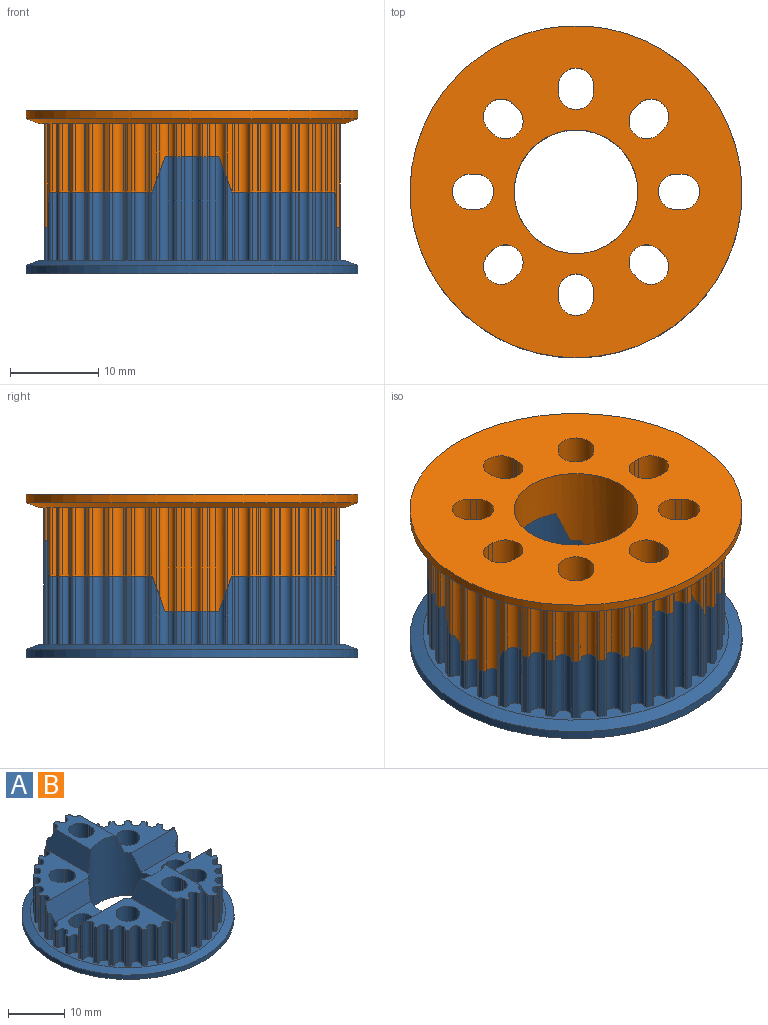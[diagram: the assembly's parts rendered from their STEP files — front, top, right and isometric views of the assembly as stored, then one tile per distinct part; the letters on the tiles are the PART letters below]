
ASSEMBLY  parts=2 mates=1
PART A: 233 faces, bbox 37.6x37.6x13.3 mm
  f0: cylinder r=2mm len=5.25mm, axis (0,0,-1), area 33mm2, adj f49,f55,f231,f232
  f1: cylinder r=2mm len=9.25mm, axis (0,0,-1), area 58.1mm2, adj f49,f53,f226,f227
  f2: cylinder r=2mm len=9.25mm, axis (0,0,-1), area 58.1mm2, adj f49,f61,f212,f213
  f3: cone r=18.8mm half-angle=70deg, axis (0,0,-1), area 181mm2, adj f4,f211
  f4: cylinder r=18.8mm len=37.6mm, axis (0,0,1), area 112.7mm2, adj f3,f49
  f5: cylinder r=0.86mm len=11.75mm, axis (0,0,1), area 17.8mm2, adj f30,f36,f59,f211
  f6: cylinder r=0.27mm len=11.75mm, axis (0,0,1), area 5.4mm2, adj f36,f59,f148,f211
  f7: cylinder r=0.27mm len=11.75mm, axis (0,0,1), area 5.4mm2, adj f29,f59,f147,f211
  f8: cylinder r=0.86mm len=11.75mm, axis (0,0,1), area 17.8mm2, adj f28,f59,f76,f211
  f9: cylinder r=0.27mm len=7.75mm, axis (0,0,1), area 3.6mm2, adj f31,f52,f141,f211
  f10: cylinder r=0.86mm len=7.75mm, axis (0,0,1), area 11.7mm2, adj f35,f61,f96,f211
  f11: cylinder r=0.27mm len=7.75mm, axis (0,0,1), area 3.6mm2, adj f26,f52,f151,f211
  f12: cylinder r=0.86mm len=7.75mm, axis (0,0,1), area 11.7mm2, adj f37,f61,f95,f211
  f13: cylinder r=0.27mm len=7.75mm, axis (0,0,1), area 3.6mm2, adj f27,f52,f155,f211
  f14: cylinder r=0.86mm len=7.75mm, axis (0,0,1), area 11.7mm2, adj f38,f61,f94,f211
  f15: cylinder r=0.27mm len=7.75mm, axis (0,0,1), area 3.6mm2, adj f33,f52,f159,f211
  f16: cylinder r=0.86mm len=7.75mm, axis (0,0,1), area 11.7mm2, adj f39,f61,f93,f211
  f17: cylinder r=0.27mm len=7.75mm, axis (0,0,1), area 3.6mm2, adj f34,f52,f163,f211
  f18: cylinder r=0.86mm len=7.75mm, axis (0,0,1), area 11.7mm2, adj f40,f61,f92,f211
  f19: cylinder r=0.27mm len=7.75mm, axis (0,0,1), area 3.6mm2, adj f32,f52,f167,f211
  f20: cylinder r=0.86mm len=7.75mm, axis (0,0,1), area 11.7mm2, adj f41,f61,f91,f211
  f21: cylinder r=0.27mm len=6.55mm, axis (0,0,1), area 2.8mm2, adj f43,f119,f138,f211
  f22: cylinder r=0.86mm len=5.64mm, axis (0,0,1), area 7.1mm2, adj f44,f55,f69,f122,f211
  f23: cylinder r=0.27mm len=3.75mm, axis (0,0,1), area 1.7mm2, adj f42,f54,f134,f211
  f24: cylinder r=0.86mm len=3.75mm, axis (0,0,1), area 5.7mm2, adj f45,f55,f67,f211
  f25: cylinder r=7mm len=14mm, axis (0,0,-1), area 406.8mm2, adj f49,f50,f51,f52,f53,f54,f55,f59
  f26: cylinder r=0.86mm len=7.75mm, axis (0,0,-1), area 11.7mm2, adj f11,f52,f153,f211
  f27: cylinder r=0.86mm len=7.75mm, axis (0,0,-1), area 11.7mm2, adj f13,f52,f157,f211
  f28: cylinder r=0.27mm len=11.75mm, axis (0,0,-1), area 5.4mm2, adj f8,f59,f148,f211
  f29: cylinder r=0.86mm len=11.75mm, axis (0,0,-1), area 17.8mm2, adj f7,f59,f142,f211
  f30: cylinder r=0.27mm len=11.75mm, axis (0,0,-1), area 5.4mm2, adj f5,f59,f147,f211
  f31: cylinder r=0.86mm len=7.75mm, axis (0,0,-1), area 11.7mm2, adj f9,f52,f149,f211
  f32: cylinder r=0.86mm len=7.75mm, axis (0,0,-1), area 11.7mm2, adj f19,f52,f169,f211
  f33: cylinder r=0.86mm len=7.75mm, axis (0,0,-1), area 11.7mm2, adj f15,f52,f161,f211
  f34: cylinder r=0.86mm len=7.75mm, axis (0,0,-1), area 11.7mm2, adj f17,f52,f165,f211
  f35: cylinder r=0.27mm len=7.75mm, axis (0,0,-1), area 3.6mm2, adj f10,f61,f145,f211
  f36: cylinder r=0.86mm len=11.75mm, axis (0,0,-1), area 17.8mm2, adj f5,f6,f59,f211
  f37: cylinder r=0.27mm len=7.75mm, axis (0,0,-1), area 3.6mm2, adj f12,f61,f152,f211
  f38: cylinder r=0.27mm len=7.75mm, axis (0,0,-1), area 3.6mm2, adj f14,f61,f156,f211
  f39: cylinder r=0.27mm len=7.75mm, axis (0,0,-1), area 3.6mm2, adj f16,f61,f160,f211
  f40: cylinder r=0.27mm len=7.75mm, axis (0,0,-1), area 3.6mm2, adj f18,f61,f164,f211
  f41: cylinder r=0.27mm len=7.75mm, axis (0,0,-1), area 3.6mm2, adj f20,f61,f168,f211
  f42: cylinder r=0.86mm len=3.75mm, axis (0,0,-1), area 5.7mm2, adj f23,f54,f132,f211
  f43: cylinder r=0.86mm len=5.64mm, axis (0,0,-1), area 7.1mm2, adj f21,f54,f119,f136,f211
  f44: cylinder r=0.27mm len=6.55mm, axis (0,0,-1), area 2.8mm2, adj f22,f122,f137,f211
  f45: cylinder r=0.27mm len=3.75mm, axis (0,0,-1), area 1.7mm2, adj f24,f55,f133,f211
  f46: cylinder r=2mm len=9.25mm, axis (0,0,-1), area 58.1mm2, adj f49,f52,f218,f219
  f47: cylinder r=2mm len=9.25mm, axis (0,0,-1), area 58.1mm2, adj f49,f51,f221,f222
  f48: cylinder r=2mm len=5.25mm, axis (0,0,-1), area 33mm2, adj f49,f54,f228,f230
  f49: plane 37.6x37.6mm, normal (0,0,-1), area 833.9mm2, adj f0,f1,f2,f4,f25,f46,f47,f48
  f50: plane 10.46x6.09mm, normal (0,0,1), area 40.4mm2, adj f25,f58,f63,f64,f65,f75,f86,f115
  f51: plane 11.69x11.69mm, normal (0,0,1), area 64.5mm2, adj f25,f47,f103,f104,f105,f106,f107,f108
  f52: plane 11.69x11.69mm, normal (0,0,1), area 64.5mm2, adj f9,f11,f13,f15,f17,f19,f25,f26
  f53: plane 11.69x11.69mm, normal (0,0,1), area 64.5mm2, adj f1,f25,f57,f78,f79,f80,f81,f82
  f54: plane 10.46x6.09mm, normal (0,0,1), area 40.4mm2, adj f23,f25,f42,f43,f48,f71,f72,f73
  f55: plane 10.46x6.09mm, normal (0,0,1), area 40.4mm2, adj f0,f22,f24,f25,f45,f56,f66,f67
  f56: cylinder r=2mm len=5.25mm, axis (0,0,-1), area 33mm2, adj f49,f55,f231,f232
  f57: cylinder r=2mm len=9.25mm, axis (0,0,-1), area 58.1mm2, adj f49,f53,f226,f227
  f58: cylinder r=2mm len=13.25mm, axis (0,0,-1), area 83.3mm2, adj f49,f50,f223,f225
  f59: plane 10.46x6.09mm, normal (0,0,1), area 40.4mm2, adj f5,f6,f7,f8,f25,f28,f29,f30
  f60: cylinder r=2mm len=13.25mm, axis (0,0,-1), area 83.3mm2, adj f49,f59,f214,f216
  f61: plane 11.69x11.69mm, normal (0,0,1), area 64.5mm2, adj f2,f10,f12,f14,f16,f18,f20,f25
  f62: cylinder r=2mm len=9.25mm, axis (0,0,-1), area 58.1mm2, adj f49,f61,f212,f213
  f63: cylinder r=0.86mm len=11.75mm, axis (0,0,-1), area 17.8mm2, adj f50,f209,f210,f211
  f64: cylinder r=0.27mm len=11.75mm, axis (0,0,-1), area 5.4mm2, adj f50,f205,f207,f211
  f65: cylinder r=0.86mm len=11.75mm, axis (0,0,-1), area 17.8mm2, adj f50,f143,f206,f211
  f66: cylinder r=0.27mm len=3.75mm, axis (0,0,-1), area 1.7mm2, adj f55,f127,f129,f211
  f67: cylinder r=0.86mm len=3.75mm, axis (0,0,-1), area 5.7mm2, adj f24,f55,f131,f211
  f68: cylinder r=0.86mm len=5.64mm, axis (0,0,-1), area 7.1mm2, adj f55,f121,f125,f127,f211
  f69: cylinder r=0.86mm len=3.75mm, axis (0,0,-1), area 5.7mm2, adj f22,f55,f135,f211
  f70: cylinder r=0.27mm len=6.55mm, axis (0,0,-1), area 2.8mm2, adj f120,f124,f126,f211
  f71: cylinder r=0.27mm len=3.75mm, axis (0,0,-1), area 1.7mm2, adj f54,f130,f132,f211
  f72: cylinder r=0.86mm len=3.75mm, axis (0,0,-1), area 5.7mm2, adj f54,f126,f128,f211
  f73: cylinder r=0.27mm len=3.75mm, axis (0,0,-1), area 1.7mm2, adj f54,f134,f136,f211
  f74: cylinder r=0.27mm len=9.86mm, axis (0,0,-1), area 4.4mm2, adj f118,f141,f142,f211
  f75: cylinder r=0.86mm len=11.75mm, axis (0,0,-1), area 16.4mm2, adj f50,f117,f139,f205,f211
  f76: cylinder r=0.86mm len=11.75mm, axis (0,0,-1), area 16.4mm2, adj f8,f59,f116,f146,f211
  f77: cylinder r=0.27mm len=9.86mm, axis (0,0,-1), area 4.4mm2, adj f115,f143,f144,f211
  f78: cylinder r=0.86mm len=7.75mm, axis (0,0,-1), area 11.7mm2, adj f53,f172,f174,f211
  f79: cylinder r=0.27mm len=7.75mm, axis (0,0,-1), area 3.6mm2, adj f53,f182,f184,f211
  f80: cylinder r=0.86mm len=7.75mm, axis (0,0,-1), area 11.7mm2, adj f53,f178,f180,f211
  f81: cylinder r=0.27mm len=7.75mm, axis (0,0,-1), area 3.6mm2, adj f53,f188,f190,f211
  f82: cylinder r=0.27mm len=7.75mm, axis (0,0,-1), area 3.6mm2, adj f53,f123,f172,f211
  f83: cylinder r=0.27mm len=7.75mm, axis (0,0,-1), area 3.6mm2, adj f53,f176,f178,f211
  f84: cylinder r=0.86mm len=7.75mm, axis (0,0,-1), area 11.7mm2, adj f53,f196,f198,f211
  f85: cylinder r=0.86mm len=7.75mm, axis (0,0,-1), area 11.7mm2, adj f53,f202,f204,f211
  f86: cylinder r=0.27mm len=11.75mm, axis (0,0,-1), area 5.4mm2, adj f50,f208,f210,f211
  f87: cylinder r=0.86mm len=7.75mm, axis (0,0,-1), area 11.7mm2, adj f53,f184,f186,f211
  f88: cylinder r=0.27mm len=7.75mm, axis (0,0,-1), area 3.6mm2, adj f53,f194,f196,f211
  f89: cylinder r=0.86mm len=7.75mm, axis (0,0,-1), area 11.7mm2, adj f53,f190,f192,f211
  f90: cylinder r=0.27mm len=7.75mm, axis (0,0,-1), area 3.6mm2, adj f53,f200,f202,f211
  f91: cylinder r=0.86mm len=7.75mm, axis (0,0,-1), area 11.7mm2, adj f20,f61,f170,f211
  f92: cylinder r=0.86mm len=7.75mm, axis (0,0,-1), area 11.7mm2, adj f18,f61,f166,f211
  f93: cylinder r=0.86mm len=7.75mm, axis (0,0,-1), area 11.7mm2, adj f16,f61,f162,f211
  f94: cylinder r=0.86mm len=7.75mm, axis (0,0,-1), area 11.7mm2, adj f14,f61,f158,f211
  f95: cylinder r=0.86mm len=7.75mm, axis (0,0,-1), area 11.7mm2, adj f12,f61,f154,f211
  f96: cylinder r=0.86mm len=7.75mm, axis (0,0,-1), area 11.7mm2, adj f10,f61,f150,f211
  f97: cylinder r=0.27mm len=7.75mm, axis (0,0,-1), area 3.6mm2, adj f52,f157,f159,f211
  f98: cylinder r=0.27mm len=7.75mm, axis (0,0,-1), area 3.6mm2, adj f52,f153,f155,f211
  f99: cylinder r=0.27mm len=7.75mm, axis (0,0,-1), area 3.6mm2, adj f52,f138,f169,f211
  f100: cylinder r=0.27mm len=7.75mm, axis (0,0,-1), area 3.6mm2, adj f52,f165,f167,f211
  f101: cylinder r=0.27mm len=7.75mm, axis (0,0,-1), area 3.6mm2, adj f52,f161,f163,f211
  f102: cylinder r=0.27mm len=7.75mm, axis (0,0,-1), area 3.6mm2, adj f52,f149,f151,f211
  f103: cylinder r=0.86mm len=7.75mm, axis (0,0,-1), area 11.7mm2, adj f51,f195,f197,f211
  f104: cylinder r=0.27mm len=7.75mm, axis (0,0,-1), area 3.6mm2, adj f51,f185,f187,f211
  f105: cylinder r=0.86mm len=7.75mm, axis (0,0,-1), area 11.7mm2, adj f51,f189,f191,f211
  f106: cylinder r=0.27mm len=7.75mm, axis (0,0,-1), area 3.6mm2, adj f51,f179,f181,f211
  f107: cylinder r=0.27mm len=7.75mm, axis (0,0,-1), area 3.6mm2, adj f51,f140,f203,f211
  f108: cylinder r=0.27mm len=7.75mm, axis (0,0,-1), area 3.6mm2, adj f51,f197,f199,f211
  f109: cylinder r=0.86mm len=7.75mm, axis (0,0,-1), area 11.7mm2, adj f51,f201,f203,f211
  f110: cylinder r=0.27mm len=7.75mm, axis (0,0,-1), area 3.6mm2, adj f51,f191,f193,f211
  f111: cylinder r=0.86mm len=7.75mm, axis (0,0,-1), area 11.7mm2, adj f51,f177,f179,f211
  f112: cylinder r=0.27mm len=7.75mm, axis (0,0,-1), area 3.6mm2, adj f51,f173,f175,f211
  f113: cylinder r=0.86mm len=7.75mm, axis (0,0,-1), area 11.7mm2, adj f51,f183,f185,f211
  f114: cylinder r=0.86mm len=7.75mm, axis (0,0,-1), area 11.7mm2, adj f51,f171,f173,f211
  f115: plane 10.95x4mm, normal (-0.94,0,0.34), area 42.6mm2, adj f25,f50,f53,f77,f143,f144
  f116: plane 10.98x4mm, normal (-0.94,0,0.34), area 42.6mm2, adj f25,f59,f61,f76,f145,f146
  f117: plane 10.98x4mm, normal (0.94,0,0.34), area 42.6mm2, adj f25,f50,f51,f75,f139,f140
  f118: plane 10.95x4mm, normal (0.94,0,0.34), area 42.6mm2, adj f25,f52,f59,f74,f141,f142
  f119: plane 10.95x4mm, normal (0,-0.94,0.34), area 42.6mm2, adj f21,f25,f43,f52,f54,f138
  f120: plane 10.95x4mm, normal (0,0.94,0.34), area 42.6mm2, adj f25,f51,f54,f70,f124,f126
  f121: plane 10.95x4mm, normal (0,0.94,0.34), area 42.6mm2, adj f25,f53,f55,f68,f123,f125
  f122: plane 10.95x4mm, normal (0,-0.94,0.34), area 42.6mm2, adj f22,f25,f44,f55,f61,f137
  f123: cylinder r=16.8mm len=7.75mm, axis (0,0,-1), area 4.3mm2, adj f53,f82,f121,f125,f211
  f124: cylinder r=16.8mm len=7.75mm, axis (0,0,-1), area 4.3mm2, adj f51,f70,f120,f171,f211
  f125: cylinder r=0.27mm len=6.55mm, axis (0,0,1), area 2.8mm2, adj f68,f121,f123,f211
  f126: cylinder r=0.86mm len=5.64mm, axis (0,0,1), area 7.1mm2, adj f54,f70,f72,f120,f211
  f127: cylinder r=0.86mm len=3.75mm, axis (0,0,1), area 5.7mm2, adj f55,f66,f68,f211
  f128: cylinder r=0.27mm len=3.75mm, axis (0,0,1), area 1.7mm2, adj f54,f72,f130,f211
  f129: cylinder r=16.8mm len=3.75mm, axis (0,0,-1), area 2.2mm2, adj f55,f66,f131,f211
  f130: cylinder r=16.8mm len=3.75mm, axis (0,0,-1), area 2.2mm2, adj f54,f71,f128,f211
  f131: cylinder r=0.27mm len=3.75mm, axis (0,0,1), area 1.7mm2, adj f55,f67,f129,f211
  f132: cylinder r=0.86mm len=3.75mm, axis (0,0,1), area 5.7mm2, adj f42,f54,f71,f211
  f133: cylinder r=16.8mm len=3.75mm, axis (0,0,-1), area 2.2mm2, adj f45,f55,f135,f211
  f134: cylinder r=16.8mm len=3.75mm, axis (0,0,-1), area 2.2mm2, adj f23,f54,f73,f211
  f135: cylinder r=0.27mm len=3.75mm, axis (0,0,1), area 1.7mm2, adj f55,f69,f133,f211
  f136: cylinder r=0.86mm len=3.75mm, axis (0,0,1), area 5.7mm2, adj f43,f54,f73,f211
  f137: cylinder r=16.8mm len=7.75mm, axis (0,0,-1), area 4.3mm2, adj f44,f61,f122,f170,f211
  f138: cylinder r=16.8mm len=7.75mm, axis (0,0,-1), area 4.3mm2, adj f21,f52,f99,f119,f211
  f139: cylinder r=0.27mm len=9.86mm, axis (0,0,1), area 4.4mm2, adj f75,f117,f140,f211
  f140: cylinder r=16.8mm len=8.95mm, axis (0,0,-1), area 4.8mm2, adj f51,f107,f117,f139,f211
  f141: cylinder r=16.8mm len=8.95mm, axis (0,0,-1), area 4.8mm2, adj f9,f52,f74,f118,f211
  f142: cylinder r=0.86mm len=11.75mm, axis (0,0,1), area 16.4mm2, adj f29,f59,f74,f118,f211
  f143: cylinder r=0.86mm len=11.75mm, axis (0,0,1), area 16.4mm2, adj f50,f65,f77,f115,f211
  f144: cylinder r=16.8mm len=8.95mm, axis (0,0,-1), area 4.8mm2, adj f53,f77,f115,f204,f211
  f145: cylinder r=16.8mm len=8.95mm, axis (0,0,-1), area 4.8mm2, adj f35,f61,f116,f146,f211
  f146: cylinder r=0.27mm len=9.86mm, axis (0,0,1), area 4.4mm2, adj f76,f116,f145,f211
  f147: cylinder r=16.8mm len=11.75mm, axis (0,0,-1), area 6.9mm2, adj f7,f30,f59,f211
  f148: cylinder r=16.8mm len=11.75mm, axis (0,0,-1), area 6.9mm2, adj f6,f28,f59,f211
  f149: cylinder r=0.86mm len=7.75mm, axis (0,0,1), area 11.7mm2, adj f31,f52,f102,f211
  f150: cylinder r=0.27mm len=7.75mm, axis (0,0,1), area 3.6mm2, adj f61,f96,f152,f211
  f151: cylinder r=16.8mm len=7.75mm, axis (0,0,-1), area 4.5mm2, adj f11,f52,f102,f211
  f152: cylinder r=16.8mm len=7.75mm, axis (0,0,-1), area 4.5mm2, adj f37,f61,f150,f211
  f153: cylinder r=0.86mm len=7.75mm, axis (0,0,1), area 11.7mm2, adj f26,f52,f98,f211
  f154: cylinder r=0.27mm len=7.75mm, axis (0,0,1), area 3.6mm2, adj f61,f95,f156,f211
  f155: cylinder r=16.8mm len=7.75mm, axis (0,0,-1), area 4.5mm2, adj f13,f52,f98,f211
  f156: cylinder r=16.8mm len=7.75mm, axis (0,0,-1), area 4.5mm2, adj f38,f61,f154,f211
  f157: cylinder r=0.86mm len=7.75mm, axis (0,0,1), area 11.7mm2, adj f27,f52,f97,f211
  f158: cylinder r=0.27mm len=7.75mm, axis (0,0,1), area 3.6mm2, adj f61,f94,f160,f211
  f159: cylinder r=16.8mm len=7.75mm, axis (0,0,-1), area 4.5mm2, adj f15,f52,f97,f211
  f160: cylinder r=16.8mm len=7.75mm, axis (0,0,-1), area 4.5mm2, adj f39,f61,f158,f211
  f161: cylinder r=0.86mm len=7.75mm, axis (0,0,1), area 11.7mm2, adj f33,f52,f101,f211
  f162: cylinder r=0.27mm len=7.75mm, axis (0,0,1), area 3.6mm2, adj f61,f93,f164,f211
  f163: cylinder r=16.8mm len=7.75mm, axis (0,0,-1), area 4.5mm2, adj f17,f52,f101,f211
  f164: cylinder r=16.8mm len=7.75mm, axis (0,0,-1), area 4.5mm2, adj f40,f61,f162,f211
  f165: cylinder r=0.86mm len=7.75mm, axis (0,0,1), area 11.7mm2, adj f34,f52,f100,f211
  f166: cylinder r=0.27mm len=7.75mm, axis (0,0,1), area 3.6mm2, adj f61,f92,f168,f211
  f167: cylinder r=16.8mm len=7.75mm, axis (0,0,-1), area 4.5mm2, adj f19,f52,f100,f211
  f168: cylinder r=16.8mm len=7.75mm, axis (0,0,-1), area 4.5mm2, adj f41,f61,f166,f211
  f169: cylinder r=0.86mm len=7.75mm, axis (0,0,1), area 11.7mm2, adj f32,f52,f99,f211
  f170: cylinder r=0.27mm len=7.75mm, axis (0,0,1), area 3.6mm2, adj f61,f91,f137,f211
  f171: cylinder r=0.27mm len=7.75mm, axis (0,0,1), area 3.6mm2, adj f51,f114,f124,f211
  f172: cylinder r=0.86mm len=7.75mm, axis (0,0,1), area 11.7mm2, adj f53,f78,f82,f211
  f173: cylinder r=0.86mm len=7.75mm, axis (0,0,1), area 11.7mm2, adj f51,f112,f114,f211
  f174: cylinder r=0.27mm len=7.75mm, axis (0,0,1), area 3.6mm2, adj f53,f78,f176,f211
  f175: cylinder r=16.8mm len=7.75mm, axis (0,0,-1), area 4.5mm2, adj f51,f112,f177,f211
  f176: cylinder r=16.8mm len=7.75mm, axis (0,0,-1), area 4.5mm2, adj f53,f83,f174,f211
  f177: cylinder r=0.27mm len=7.75mm, axis (0,0,1), area 3.6mm2, adj f51,f111,f175,f211
  f178: cylinder r=0.86mm len=7.75mm, axis (0,0,1), area 11.7mm2, adj f53,f80,f83,f211
  f179: cylinder r=0.86mm len=7.75mm, axis (0,0,1), area 11.7mm2, adj f51,f106,f111,f211
  f180: cylinder r=0.27mm len=7.75mm, axis (0,0,1), area 3.6mm2, adj f53,f80,f182,f211
  f181: cylinder r=16.8mm len=7.75mm, axis (0,0,-1), area 4.5mm2, adj f51,f106,f183,f211
  f182: cylinder r=16.8mm len=7.75mm, axis (0,0,-1), area 4.5mm2, adj f53,f79,f180,f211
  f183: cylinder r=0.27mm len=7.75mm, axis (0,0,1), area 3.6mm2, adj f51,f113,f181,f211
  f184: cylinder r=0.86mm len=7.75mm, axis (0,0,1), area 11.7mm2, adj f53,f79,f87,f211
  f185: cylinder r=0.86mm len=7.75mm, axis (0,0,1), area 11.7mm2, adj f51,f104,f113,f211
  f186: cylinder r=0.27mm len=7.75mm, axis (0,0,1), area 3.6mm2, adj f53,f87,f188,f211
  f187: cylinder r=16.8mm len=7.75mm, axis (0,0,-1), area 4.5mm2, adj f51,f104,f189,f211
  f188: cylinder r=16.8mm len=7.75mm, axis (0,0,-1), area 4.5mm2, adj f53,f81,f186,f211
  f189: cylinder r=0.27mm len=7.75mm, axis (0,0,1), area 3.6mm2, adj f51,f105,f187,f211
  f190: cylinder r=0.86mm len=7.75mm, axis (0,0,1), area 11.7mm2, adj f53,f81,f89,f211
  f191: cylinder r=0.86mm len=7.75mm, axis (0,0,1), area 11.7mm2, adj f51,f105,f110,f211
  f192: cylinder r=0.27mm len=7.75mm, axis (0,0,1), area 3.6mm2, adj f53,f89,f194,f211
  f193: cylinder r=16.8mm len=7.75mm, axis (0,0,-1), area 4.5mm2, adj f51,f110,f195,f211
  f194: cylinder r=16.8mm len=7.75mm, axis (0,0,-1), area 4.5mm2, adj f53,f88,f192,f211
  f195: cylinder r=0.27mm len=7.75mm, axis (0,0,1), area 3.6mm2, adj f51,f103,f193,f211
  f196: cylinder r=0.86mm len=7.75mm, axis (0,0,1), area 11.7mm2, adj f53,f84,f88,f211
  f197: cylinder r=0.86mm len=7.75mm, axis (0,0,1), area 11.7mm2, adj f51,f103,f108,f211
  f198: cylinder r=0.27mm len=7.75mm, axis (0,0,1), area 3.6mm2, adj f53,f84,f200,f211
  f199: cylinder r=16.8mm len=7.75mm, axis (0,0,-1), area 4.5mm2, adj f51,f108,f201,f211
  f200: cylinder r=16.8mm len=7.75mm, axis (0,0,-1), area 4.5mm2, adj f53,f90,f198,f211
  f201: cylinder r=0.27mm len=7.75mm, axis (0,0,1), area 3.6mm2, adj f51,f109,f199,f211
  f202: cylinder r=0.86mm len=7.75mm, axis (0,0,1), area 11.7mm2, adj f53,f85,f90,f211
  f203: cylinder r=0.86mm len=7.75mm, axis (0,0,1), area 11.7mm2, adj f51,f107,f109,f211
  f204: cylinder r=0.27mm len=7.75mm, axis (0,0,1), area 3.6mm2, adj f53,f85,f144,f211
  f205: cylinder r=0.86mm len=11.75mm, axis (0,0,1), area 17.8mm2, adj f50,f64,f75,f211
  f206: cylinder r=0.27mm len=11.75mm, axis (0,0,1), area 5.4mm2, adj f50,f65,f208,f211
  f207: cylinder r=16.8mm len=11.75mm, axis (0,0,-1), area 6.9mm2, adj f50,f64,f209,f211
  f208: cylinder r=16.8mm len=11.75mm, axis (0,0,-1), area 6.9mm2, adj f50,f86,f206,f211
  f209: cylinder r=0.27mm len=11.75mm, axis (0,0,1), area 5.4mm2, adj f50,f63,f207,f211
  f210: cylinder r=0.86mm len=11.75mm, axis (0,0,1), area 17.8mm2, adj f50,f63,f86,f211
  f211: plane 34.6x34.6mm, normal (0,0,1), area 127.6mm2, adj f3,f5,f6,f7,f8,f9,f10,f11
  f212: plane 9.25x0.49mm, normal (-0.71,-0.71,0), area 6.3mm2, adj f2,f49,f61,f62
  f213: plane 9.25x0.49mm, normal (0.71,0.71,0), area 6.3mm2, adj f2,f49,f61,f62
  f214: plane 13.25x0.69mm, normal (-1,0,0), area 9.1mm2, adj f49,f59,f60,f215
  f215: cylinder r=2mm len=13.25mm, axis (0,0,-1), area 83.3mm2, adj f49,f59,f214,f216
  f216: plane 13.25x0.69mm, normal (1,0,0), area 9.1mm2, adj f49,f59,f60,f215
  f217: cylinder r=2mm len=9.25mm, axis (0,0,-1), area 58.1mm2, adj f49,f52,f218,f219
  f218: plane 9.25x0.49mm, normal (-0.71,0.71,0), area 6.3mm2, adj f46,f49,f52,f217
  f219: plane 9.25x0.49mm, normal (0.71,-0.71,0), area 6.3mm2, adj f46,f49,f52,f217
  f220: cylinder r=2mm len=9.25mm, axis (0,0,-1), area 58.1mm2, adj f49,f51,f221,f222
  f221: plane 9.25x0.49mm, normal (0.71,0.71,0), area 6.3mm2, adj f47,f49,f51,f220
  f222: plane 9.25x0.49mm, normal (-0.71,-0.71,0), area 6.3mm2, adj f47,f49,f51,f220
  f223: plane 13.25x0.69mm, normal (1,0,0), area 9.1mm2, adj f49,f50,f58,f224
  f224: cylinder r=2mm len=13.25mm, axis (0,0,-1), area 83.3mm2, adj f49,f50,f223,f225
  f225: plane 13.25x0.69mm, normal (-1,0,0), area 9.1mm2, adj f49,f50,f58,f224
  f226: plane 9.25x0.49mm, normal (0.71,-0.71,0), area 6.3mm2, adj f1,f49,f53,f57
  f227: plane 9.25x0.49mm, normal (-0.71,0.71,0), area 6.3mm2, adj f1,f49,f53,f57
  f228: plane 5.25x0.69mm, normal (0,1,0), area 3.6mm2, adj f48,f49,f54,f229
  f229: cylinder r=2mm len=5.25mm, axis (0,0,-1), area 33mm2, adj f49,f54,f228,f230
  f230: plane 5.25x0.69mm, normal (0,-1,0), area 3.6mm2, adj f48,f49,f54,f229
  f231: plane 5.25x0.69mm, normal (0,-1,0), area 3.6mm2, adj f0,f49,f55,f56
  f232: plane 5.25x0.69mm, normal (0,1,0), area 3.6mm2, adj f0,f49,f55,f56
PART B: same geometry as A
PLACE A t=(-11.59,-10.63,-0.73)mm
PLACE B rot(axis=(0.71,0.71,0),180deg) t=(-11.59,-10.63,-5.83)mm
MATE fastened B.f3 <-> A.f3  axis (0,0,-1) through (-11.59,-10.63,-7.28)mm
